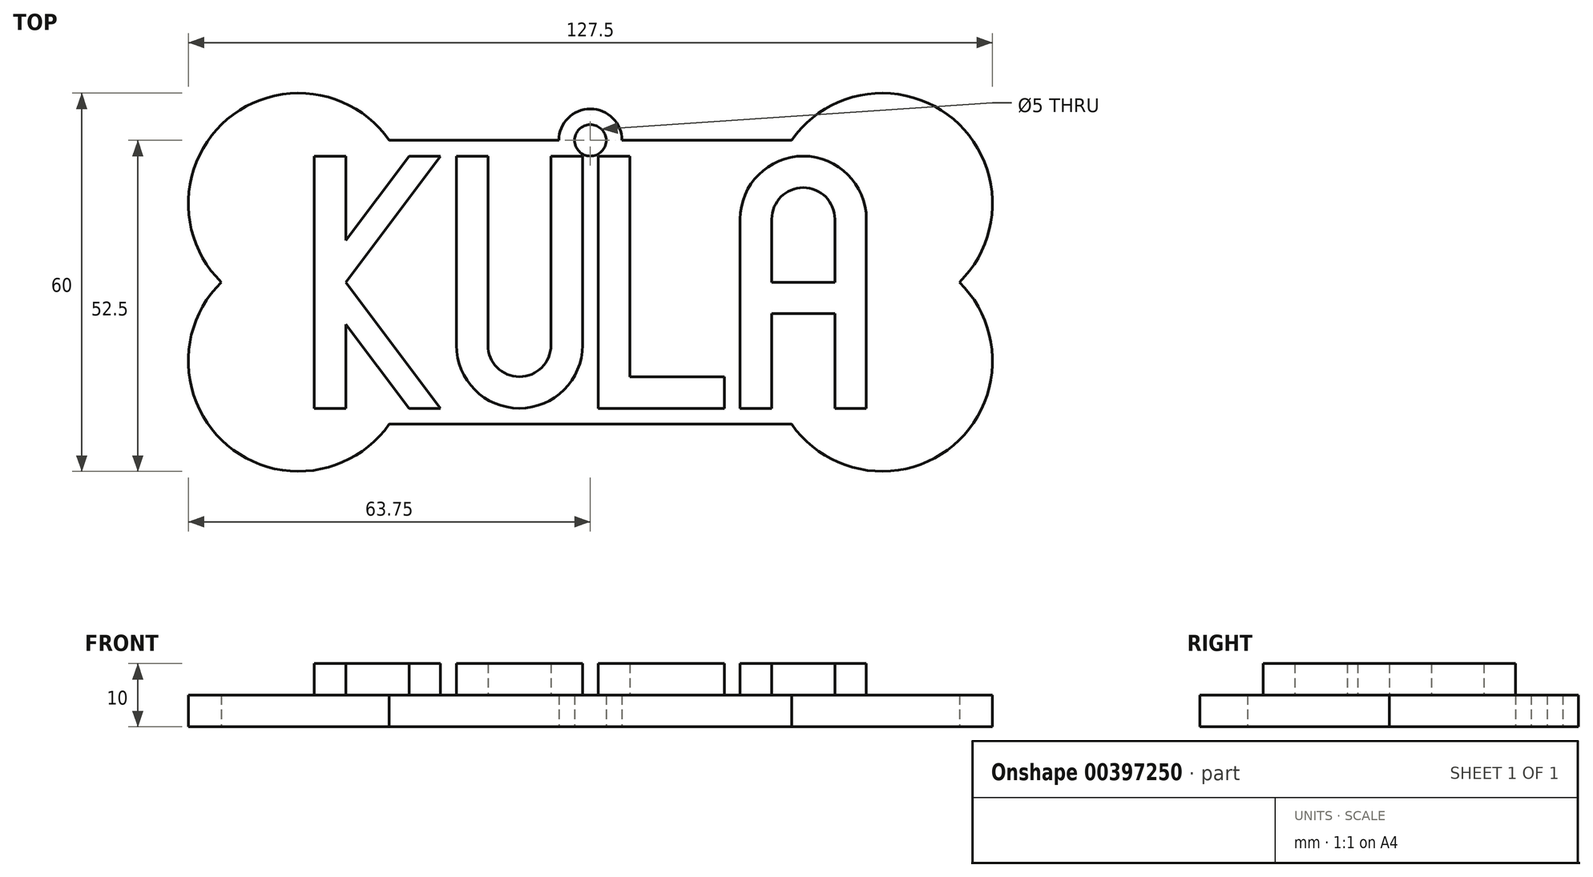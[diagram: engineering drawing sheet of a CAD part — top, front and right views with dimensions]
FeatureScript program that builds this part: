
annotation { "Feature Type Name" : "Feature", "Feature Type Description" : "" }
export const myFeature = defineFeature(function(context is Context, id is Id, definition is map)
    precondition{}
    {
        {
            var Q0;
            Q0=qCreatedBy(makeId("Top.planeOp"),FACE);
            var sketch = newSketch(context, id + "F0", { "sketchPlane" : qUnion([Q0])});
            skLineSegment(sketch, "E0.bottom", {"start": v(-90, 42.5) * mm, "end": v(-70, 42.5) * mm});
            skLineSegment(sketch, "E0.top", {"start": v(-90, 2.5) * mm, "end": v(-70, 2.5) * mm});
            skLineSegment(sketch, "E0.left", {"start": v(-90, 42.5) * mm, "end": v(-90, 2.5) * mm});
            skLineSegment(sketch, "E0.right", {"start": v(-70, 42.5) * mm, "end": v(-70, 2.5) * mm});
            skLineSegment(sketch, "E1.bottom", {"start": v(-67.5, 42.5) * mm, "end": v(-47.5, 42.5) * mm});
            skLineSegment(sketch, "E1.top", {"start": v(-67.5, 2.5) * mm, "end": v(-47.5, 2.5) * mm});
            skLineSegment(sketch, "E1.left", {"start": v(-67.5, 42.5) * mm, "end": v(-67.5, 2.5) * mm});
            skLineSegment(sketch, "E1.right", {"start": v(-47.5, 42.5) * mm, "end": v(-47.5, 2.5) * mm});
            skLineSegment(sketch, "E2.bottom", {"start": v(-22.5, 42.5) * mm, "end": v(-2.5, 42.5) * mm});
            skLineSegment(sketch, "E2.top", {"start": v(-22.5, 2.5) * mm, "end": v(-2.5, 2.5) * mm});
            skLineSegment(sketch, "E2.left", {"start": v(-22.5, 42.5) * mm, "end": v(-22.5, 2.5) * mm});
            skLineSegment(sketch, "E2.right", {"start": v(-2.5, 42.5) * mm, "end": v(-2.5, 2.5) * mm});
            skLineSegment(sketch, "E3.bottom", {"start": v(-92.5, 45) * mm, "end": v(0, 45) * mm});
            skLineSegment(sketch, "E3.top", {"start": v(-92.5, 0) * mm, "end": v(0, 0) * mm});
            skLineSegment(sketch, "E3.left", {"start": v(-92.5, 45) * mm, "end": v(-92.5, 0) * mm});
            skLineSegment(sketch, "E3.right", {"start": v(0, 45) * mm, "end": v(0, 0) * mm});
            skLineSegment(sketch, "E4.bottom", {"start": v(-45, 42.5) * mm, "end": v(-25, 42.5) * mm});
            skLineSegment(sketch, "E4.top", {"start": v(-45, 2.5) * mm, "end": v(-25, 2.5) * mm});
            skLineSegment(sketch, "E4.left", {"start": v(-45, 42.5) * mm, "end": v(-45, 2.5) * mm});
            skLineSegment(sketch, "E4.right", {"start": v(-25, 42.5) * mm, "end": v(-25, 2.5) * mm});
            skPoint(sketch, "E5", {"position": v(-92.5, 35) * mm});
            skPoint(sketch, "E6", {"position": v(-92.5, 10) * mm});
            skPoint(sketch, "E7", {"position": v(0, 10) * mm});
            skPoint(sketch, "E8", {"position": v(0, 35) * mm});
            skCircle(sketch, "E9", {"center": v(-92.5, 35) * mm, "radius": 17.5 * mm});
            skCircle(sketch, "E10", {"center": v(-92.5, 10) * mm, "radius": 17.5 * mm});
            skCircle(sketch, "E11", {"center": v(0, 35) * mm, "radius": 17.5 * mm});
            skCircle(sketch, "E12", {"center": v(0, 10) * mm, "radius": 17.5 * mm});
            skPoint(sketch, "E13", {"position": v(-46.25, 45) * mm});
            skCircle(sketch, "E14", {"center": v(-46.25, 45) * mm, "radius": 2.5 * mm});
            skCircle(sketch, "E15", {"center": v(-46.25, 45) * mm, "radius": 5 * mm});
            skSolve(sketch);
        }
        {
            var Q0;
            {var subQ0=sQuery(id+"F0.wireOp",EDGE,"E3.left");var subQ1=sQuery(id+"F0.wireOp",EDGE,"E3.bottom");var subQ2=makeQuery(id+"F0.imprint","INTERSECT",VERTEX,{"derivedFrom":[subQ1,subQ0]});Q0=makeQuery(id+"F0.imprint","IMPRINT",FACE,{"disambiguationData":[TD([[makeQuery(id+"F0.imprint","IMPRINT",EDGE,{"disambiguationData":[TD([[subQ2,-1.0]])],"derivedFrom":subQ1}),1.0]])]});}
            var Q1;
            {var subQ0=sQuery(id+"F0.wireOp",EDGE,"E10");var subQ1=sQuery(id+"F0.wireOp",EDGE,"E3.left");var subQ2=makeQuery(id+"F0.imprint","INTERSECT",VERTEX,{"derivedFrom":[subQ1,subQ0]});Q1=makeQuery(id+"F0.imprint","IMPRINT",FACE,{"disambiguationData":[TD([[makeQuery(id+"F0.imprint","IMPRINT",EDGE,{"disambiguationData":[TD([[subQ2,-1.0]])],"derivedFrom":subQ1}),-1.0]])]});}
            var Q2;
            {var subQ0=sQuery(id+"F0.wireOp",EDGE,"E3.left");var subQ1=sQuery(id+"F0.wireOp",EDGE,"E3.top");var subQ2=makeQuery(id+"F0.imprint","INTERSECT",VERTEX,{"derivedFrom":[subQ1,subQ0]});Q2=makeQuery(id+"F0.imprint","IMPRINT",FACE,{"disambiguationData":[TD([[makeQuery(id+"F0.imprint","IMPRINT",EDGE,{"disambiguationData":[TD([[subQ2,-1.0]])],"derivedFrom":subQ1}),-1.0]])]});}
            var Q3;
            {var subQ0=sQuery(id+"F0.wireOp",EDGE,"E10");var subQ1=sQuery(id+"F0.wireOp",EDGE,"E0.left");var subQ2=makeQuery(id+"F0.imprint","INTERSECT",VERTEX,{"derivedFrom":[subQ1,subQ0]});Q3=makeQuery(id+"F0.imprint","IMPRINT",FACE,{"disambiguationData":[TD([[makeQuery(id+"F0.imprint","IMPRINT",EDGE,{"disambiguationData":[TD([[subQ2,-1.0]])],"derivedFrom":subQ1}),-1.0]])]});}
            var Q4;
            {var subQ5=sQuery(id+"F0.wireOp",EDGE,"E0.left");var subQ6=sQuery(id+"F0.wireOp",EDGE,"E0.bottom");var subQ7=makeQuery(id+"F0.imprint","INTERSECT",VERTEX,{"derivedFrom":[subQ6,subQ5]});Q4=makeQuery(id+"F0.imprint","IMPRINT",FACE,{"disambiguationData":[TD([[makeQuery(id+"F0.imprint","IMPRINT",EDGE,{"disambiguationData":[TD([[subQ7,-1.0]])],"derivedFrom":subQ6}),1.0]])]});}
            var Q5;
            {var subQ0=sQuery(id+"F0.wireOp",EDGE,"E0.left");var subQ1=sQuery(id+"F0.wireOp",EDGE,"E0.bottom");var subQ2=makeQuery(id+"F0.imprint","INTERSECT",VERTEX,{"derivedFrom":[subQ1,subQ0]});Q5=makeQuery(id+"F0.imprint","IMPRINT",FACE,{"disambiguationData":[TD([[makeQuery(id+"F0.imprint","IMPRINT",EDGE,{"disambiguationData":[TD([[subQ2,-1.0]])],"derivedFrom":subQ1}),-1.0]])]});}
            var Q6;
            {var subQ0=sQuery(id+"F0.wireOp",EDGE,"E10");var subQ1=sQuery(id+"F0.wireOp",EDGE,"E0.left");var subQ2=makeQuery(id+"F0.imprint","INTERSECT",VERTEX,{"derivedFrom":[subQ1,subQ0]});Q6=makeQuery(id+"F0.imprint","IMPRINT",FACE,{"disambiguationData":[TD([[makeQuery(id+"F0.imprint","IMPRINT",EDGE,{"disambiguationData":[TD([[subQ2,-1.0]])],"derivedFrom":subQ1}),1.0]])]});}
            var Q7;
            {var subQ0=sQuery(id+"F0.wireOp",EDGE,"E0.left");var subQ1=sQuery(id+"F0.wireOp",EDGE,"E0.top");var subQ2=makeQuery(id+"F0.imprint","INTERSECT",VERTEX,{"derivedFrom":[subQ1,subQ0]});Q7=makeQuery(id+"F0.imprint","IMPRINT",FACE,{"disambiguationData":[TD([[makeQuery(id+"F0.imprint","IMPRINT",EDGE,{"disambiguationData":[TD([[subQ2,-1.0]])],"derivedFrom":subQ1}),1.0]])]});}
            var Q8;
            {var subQ5=sQuery(id+"F0.wireOp",EDGE,"E0.left");var subQ6=sQuery(id+"F0.wireOp",EDGE,"E0.top");var subQ7=makeQuery(id+"F0.imprint","INTERSECT",VERTEX,{"derivedFrom":[subQ6,subQ5]});Q8=makeQuery(id+"F0.imprint","IMPRINT",FACE,{"disambiguationData":[TD([[makeQuery(id+"F0.imprint","IMPRINT",EDGE,{"disambiguationData":[TD([[subQ7,-1.0]])],"derivedFrom":subQ6}),-1.0]])]});}
            var Q9;
            {var subQ0=sQuery(id+"F0.wireOp",EDGE,"E0.right");Q9=makeQuery(id+"F0.imprint","IMPRINT",FACE,{"disambiguationData":[TD([[makeQuery(id+"F0.imprint","IMPRINT",EDGE,{"derivedFrom":subQ0}),-1.0]])]});}
            var Q10;
            {var subQ9=sQuery(id+"F0.wireOp",EDGE,"E0.right");Q10=makeQuery(id+"F0.imprint","IMPRINT",FACE,{"disambiguationData":[TD([[makeQuery(id+"F0.imprint","IMPRINT",EDGE,{"derivedFrom":subQ9}),1.0]])]});}
            var Q11;
            Q11=makeQuery(id+"F0.imprint","IMPRINT",FACE,{"disambiguationData":[TD([[makeQuery(id+"F0.imprint","IMPRINT",EDGE,{"derivedFrom":sQuery(id+"F0.wireOp",EDGE,"E1.bottom")}),-1.0]])]});
            var Q12;
            Q12=makeQuery(id+"F0.imprint","IMPRINT",FACE,{"disambiguationData":[TD([[makeQuery(id+"F0.imprint","IMPRINT",EDGE,{"derivedFrom":sQuery(id+"F0.wireOp",EDGE,"E4.bottom")}),-1.0]])]});
            var Q13;
            {var subQ0=sQuery(id+"F0.wireOp",EDGE,"E2.left");Q13=makeQuery(id+"F0.imprint","IMPRINT",FACE,{"disambiguationData":[TD([[makeQuery(id+"F0.imprint","IMPRINT",EDGE,{"derivedFrom":subQ0}),1.0]])]});}
            var Q14;
            {var subQ0=sQuery(id+"F0.wireOp",EDGE,"E2.right");var subQ1=sQuery(id+"F0.wireOp",EDGE,"E2.bottom");var subQ2=makeQuery(id+"F0.imprint","INTERSECT",VERTEX,{"derivedFrom":[subQ1,subQ0]});Q14=makeQuery(id+"F0.imprint","IMPRINT",FACE,{"disambiguationData":[TD([[makeQuery(id+"F0.imprint","IMPRINT",EDGE,{"disambiguationData":[TD([[subQ2,1.0]])],"derivedFrom":subQ1}),-1.0]])]});}
            var Q15;
            {var subQ0=sQuery(id+"F0.wireOp",EDGE,"E3.right");var subQ1=sQuery(id+"F0.wireOp",EDGE,"E3.bottom");var subQ2=makeQuery(id+"F0.imprint","INTERSECT",VERTEX,{"derivedFrom":[subQ1,subQ0]});Q15=makeQuery(id+"F0.imprint","IMPRINT",FACE,{"disambiguationData":[TD([[makeQuery(id+"F0.imprint","IMPRINT",EDGE,{"disambiguationData":[TD([[subQ2,1.0]])],"derivedFrom":subQ1}),1.0]])]});}
            var Q16;
            {var subQ0=sQuery(id+"F0.wireOp",EDGE,"E3.right");var subQ1=sQuery(id+"F0.wireOp",EDGE,"E3.top");var subQ2=makeQuery(id+"F0.imprint","INTERSECT",VERTEX,{"derivedFrom":[subQ1,subQ0]});Q16=makeQuery(id+"F0.imprint","IMPRINT",FACE,{"disambiguationData":[TD([[makeQuery(id+"F0.imprint","IMPRINT",EDGE,{"disambiguationData":[TD([[subQ2,1.0]])],"derivedFrom":subQ1}),-1.0]])]});}
            var Q17;
            {var subQ0=sQuery(id+"F0.wireOp",EDGE,"E2.right");var subQ1=sQuery(id+"F0.wireOp",EDGE,"E2.top");var subQ2=makeQuery(id+"F0.imprint","INTERSECT",VERTEX,{"derivedFrom":[subQ1,subQ0]});Q17=makeQuery(id+"F0.imprint","IMPRINT",FACE,{"disambiguationData":[TD([[makeQuery(id+"F0.imprint","IMPRINT",EDGE,{"disambiguationData":[TD([[subQ2,1.0]])],"derivedFrom":subQ1}),1.0]])]});}
            var Q18;
            {var subQ0=sQuery(id+"F0.wireOp",EDGE,"E12");var subQ1=sQuery(id+"F0.wireOp",EDGE,"E2.right");var subQ2=makeQuery(id+"F0.imprint","INTERSECT",VERTEX,{"derivedFrom":[subQ1,subQ0]});Q18=makeQuery(id+"F0.imprint","IMPRINT",FACE,{"disambiguationData":[TD([[makeQuery(id+"F0.imprint","IMPRINT",EDGE,{"disambiguationData":[TD([[subQ2,-1.0]])],"derivedFrom":subQ1}),-1.0]])]});}
            var Q19;
            {var subQ0=sQuery(id+"F0.wireOp",EDGE,"E12");var subQ1=sQuery(id+"F0.wireOp",EDGE,"E3.right");var subQ2=makeQuery(id+"F0.imprint","INTERSECT",VERTEX,{"derivedFrom":[subQ1,subQ0]});Q19=makeQuery(id+"F0.imprint","IMPRINT",FACE,{"disambiguationData":[TD([[makeQuery(id+"F0.imprint","IMPRINT",EDGE,{"disambiguationData":[TD([[subQ2,-1.0]])],"derivedFrom":subQ1}),1.0]])]});}
            var Q20;
            {var subQ5=sQuery(id+"F0.wireOp",EDGE,"E2.right");var subQ6=sQuery(id+"F0.wireOp",EDGE,"E2.top");var subQ7=makeQuery(id+"F0.imprint","INTERSECT",VERTEX,{"derivedFrom":[subQ6,subQ5]});Q20=makeQuery(id+"F0.imprint","IMPRINT",FACE,{"disambiguationData":[TD([[makeQuery(id+"F0.imprint","IMPRINT",EDGE,{"disambiguationData":[TD([[subQ7,1.0]])],"derivedFrom":subQ6}),-1.0]])]});}
            var Q21;
            {var subQ7=sQuery(id+"F0.wireOp",EDGE,"E2.right");var subQ9=sQuery(id+"F0.wireOp",EDGE,"E2.bottom");var subQ10=makeQuery(id+"F0.imprint","INTERSECT",VERTEX,{"derivedFrom":[subQ9,subQ7]});Q21=makeQuery(id+"F0.imprint","IMPRINT",FACE,{"disambiguationData":[TD([[makeQuery(id+"F0.imprint","IMPRINT",EDGE,{"disambiguationData":[TD([[subQ10,1.0]])],"derivedFrom":subQ9}),1.0]])]});}
            var Q22;
            {var subQ0=sQuery(id+"F0.wireOp",EDGE,"E12");var subQ1=sQuery(id+"F0.wireOp",EDGE,"E2.right");var subQ2=makeQuery(id+"F0.imprint","INTERSECT",VERTEX,{"derivedFrom":[subQ1,subQ0]});Q22=makeQuery(id+"F0.imprint","IMPRINT",FACE,{"disambiguationData":[TD([[makeQuery(id+"F0.imprint","IMPRINT",EDGE,{"disambiguationData":[TD([[subQ2,-1.0]])],"derivedFrom":subQ1}),1.0]])]});}
            var Q23;
            {var subQ5=sQuery(id+"F0.wireOp",EDGE,"E1.right");var subQ6=sQuery(id+"F0.wireOp",EDGE,"E1.bottom");var subQ7=makeQuery(id+"F0.imprint","INTERSECT",VERTEX,{"derivedFrom":[subQ6,subQ5]});Q23=makeQuery(id+"F0.imprint","IMPRINT",FACE,{"disambiguationData":[TD([[makeQuery(id+"F0.imprint","IMPRINT",EDGE,{"disambiguationData":[TD([[subQ7,1.0]])],"derivedFrom":subQ6}),1.0]])]});}
            var Q24;
            {var subQ0=sQuery(id+"F0.wireOp",EDGE,"E15");var subQ1=sQuery(id+"F0.wireOp",EDGE,"E3.bottom");var subQ2=makeQuery(id+"F0.imprint","INTERSECT",VERTEX,{"disambiguationData":[OD(0.0)],"derivedFrom":[subQ1,subQ0]});Q24=makeQuery(id+"F0.imprint","IMPRINT",FACE,{"disambiguationData":[TD([[makeQuery(id+"F0.imprint","IMPRINT",EDGE,{"disambiguationData":[TD([[subQ2,-1.0]])],"derivedFrom":subQ1}),1.0]])]});}
            var Q25;
            {var subQ1=sQuery(id+"F0.wireOp",EDGE,"E1.top");Q25=makeQuery(id+"F0.imprint","IMPRINT",FACE,{"disambiguationData":[TD([[makeQuery(id+"F0.imprint","IMPRINT",EDGE,{"derivedFrom":subQ1}),1.0]])]});}
            var Q26;
            {var subQ2=sQuery(id+"F0.wireOp",EDGE,"E4.top");Q26=makeQuery(id+"F0.imprint","IMPRINT",FACE,{"disambiguationData":[TD([[makeQuery(id+"F0.imprint","IMPRINT",EDGE,{"derivedFrom":subQ2}),1.0]])]});}
            extrude(context, id + "F1", {"entities" : qUnion([Q0, Q1, Q2, Q3, Q4, Q5, Q6, Q7, Q8, Q9, Q10, Q11, Q12, Q13, Q14, Q15, Q16, Q17, Q18, Q19, Q20, Q21, Q22, Q23, Q24, Q25, Q26]), "depth" : 5 * mm});
        }
        {
            var Q0;
            Q0=makeQuery(id+"F1.opExtrude","CAP_FACE",FACE,{"disambiguationData":[OSD([sQuery(id+"F0.wireOp",EDGE,"E3.bottom"),sQuery(id+"F0.wireOp",EDGE,"E3.top"),sQuery(id+"F0.wireOp",EDGE,"E9"),sQuery(id+"F0.wireOp",EDGE,"E10"),sQuery(id+"F0.wireOp",EDGE,"E11"),sQuery(id+"F0.wireOp",EDGE,"E12")])],"isStart":false});
            var sketch = newSketch(context, id + "F2", { "sketchPlane" : qUnion([Q0])});
            skLineSegment(sketch, "E16.bottom", {"start": v(-90, 42.5) * mm, "end": v(-70, 42.5) * mm});
            skLineSegment(sketch, "E16.top", {"start": v(-90, 2.5) * mm, "end": v(-70, 2.5) * mm});
            skLineSegment(sketch, "E16.left", {"start": v(-90, 42.5) * mm, "end": v(-90, 2.5) * mm});
            skLineSegment(sketch, "E17.bottom", {"start": v(-67.5, 42.5) * mm, "end": v(-47.5, 42.5) * mm});
            skLineSegment(sketch, "E17.top", {"start": v(-67.5, 2.5) * mm, "end": v(-47.5, 2.5) * mm});
            skLineSegment(sketch, "E17.left", {"start": v(-67.5, 42.5) * mm, "end": v(-67.5, 2.5) * mm});
            skLineSegment(sketch, "E17.right", {"start": v(-47.5, 42.5) * mm, "end": v(-47.5, 2.5) * mm});
            skLineSegment(sketch, "E18.bottom", {"start": v(-22.5, 42.5) * mm, "end": v(-2.5, 42.5) * mm});
            skLineSegment(sketch, "E18.top", {"start": v(-22.5, 2.5) * mm, "end": v(-2.5, 2.5) * mm});
            skLineSegment(sketch, "E18.left", {"start": v(-22.5, 42.5) * mm, "end": v(-22.5, 2.5) * mm});
            skLineSegment(sketch, "E18.right", {"start": v(-2.5, 42.5) * mm, "end": v(-2.5, 2.5) * mm});
            skLineSegment(sketch, "E19.bottom", {"start": v(-92.5, 45) * mm, "end": v(0, 45) * mm});
            skLineSegment(sketch, "E19.top", {"start": v(-92.5, 0) * mm, "end": v(0, 0) * mm});
            skLineSegment(sketch, "E19.left", {"start": v(-92.5, 45) * mm, "end": v(-92.5, 0) * mm});
            skLineSegment(sketch, "E19.right", {"start": v(0, 45) * mm, "end": v(0, 0) * mm});
            skLineSegment(sketch, "E20.bottom", {"start": v(-45, 42.5) * mm, "end": v(-25, 42.5) * mm});
            skLineSegment(sketch, "E20.top", {"start": v(-45, 2.5) * mm, "end": v(-25, 2.5) * mm});
            skLineSegment(sketch, "E20.left", {"start": v(-45, 42.5) * mm, "end": v(-45, 2.5) * mm});
            skLineSegment(sketch, "E21", {"start": v(-70, 42.5) * mm, "end": v(-70, 2.5) * mm});
            skLineSegment(sketch, "E22", {"start": v(-25, 42.5) * mm, "end": v(-25, 2.5) * mm});
            skLineSegment(sketch, "E23", {"start": v(-85, 42.5) * mm, "end": v(-85, 2.5) * mm});
            skLineSegment(sketch, "E24", {"start": v(-62.5, 42.5) * mm, "end": v(-62.5, 2.5) * mm});
            skLineSegment(sketch, "E25", {"start": v(-40, 2.5) * mm, "end": v(-40, 42.5) * mm});
            skLineSegment(sketch, "E26", {"start": v(-45, 7.5) * mm, "end": v(-25, 7.5) * mm});
            skLineSegment(sketch, "E27", {"start": v(-17.5, 42.5) * mm, "end": v(-17.5, 2.5) * mm});
            skLineSegment(sketch, "E28", {"start": v(-22.5, 22.5) * mm, "end": v(-2.5, 22.5) * mm, "construction": true});
            skLineSegment(sketch, "E29", {"start": v(-2.5, 42.5) * mm, "end": v(-22.5, 22.5) * mm, "construction": true});
            skLineSegment(sketch, "E30", {"start": v(-22.5, 42.5) * mm, "end": v(-2.5, 22.5) * mm, "construction": true});
            skCircle(sketch, "E31", {"center": v(-12.5, 32.5) * mm, "radius": 10 * mm});
            skCircle(sketch, "E32", {"center": v(-12.5, 32.5) * mm, "radius": 5 * mm});
            skLineSegment(sketch, "E33", {"start": v(-52.5, 42.5) * mm, "end": v(-52.5, 2.5) * mm});
            skLineSegment(sketch, "E34", {"start": v(-67.5, 22.5) * mm, "end": v(-47.5, 22.5) * mm, "construction": true});
            skLineSegment(sketch, "E35", {"start": v(-67.5, 22.5) * mm, "end": v(-47.5, 2.5) * mm, "construction": true});
            skLineSegment(sketch, "E36", {"start": v(-47.5, 22.5) * mm, "end": v(-67.5, 2.5) * mm, "construction": true});
            skLineSegment(sketch, "E37", {"start": v(-7.5, 42.5) * mm, "end": v(-7.5, 2.5) * mm});
            skLineSegment(sketch, "E38", {"start": v(-22.5, 22.5) * mm, "end": v(-2.5, 22.5) * mm});
            skLineSegment(sketch, "E39", {"start": v(-22.5, 17.5) * mm, "end": v(-2.5, 17.5) * mm});
            skCircle(sketch, "E40", {"center": v(-57.5, 12.5) * mm, "radius": 10 * mm});
            skCircle(sketch, "E41", {"center": v(-57.5, 12.5) * mm, "radius": 5 * mm});
            skLineSegment(sketch, "E42", {"start": v(-90, 22.5) * mm, "end": v(-70, 22.5) * mm, "construction": true});
            skLineSegment(sketch, "E43", {"start": v(-70, 42.5) * mm, "end": v(-85, 22.5) * mm});
            skLineSegment(sketch, "E44", {"start": v(-85, 22.5) * mm, "end": v(-70, 2.5) * mm});
            skLineSegment(sketch, "E45", {"start": v(-90, 22.5) * mm, "end": v(-75, 2.5) * mm});
            skLineSegment(sketch, "E46", {"start": v(-90, 22.5) * mm, "end": v(-75, 42.5) * mm});
            skSolve(sketch);
        }
        {
            var Q0;
            {var subQ0=sQuery(id+"F2.wireOp",EDGE,"E16.left");var subQ1=sQuery(id+"F2.wireOp",EDGE,"E16.bottom");var subQ2=makeQuery(id+"F2.imprint","INTERSECT",VERTEX,{"derivedFrom":[subQ1,subQ0]});Q0=makeQuery(id+"F2.imprint","IMPRINT",FACE,{"disambiguationData":[TD([[makeQuery(id+"F2.imprint","IMPRINT",EDGE,{"disambiguationData":[TD([[subQ2,-1.0]])],"derivedFrom":subQ1}),-1.0]])]});}
            var Q1;
            {var subQ0=sQuery(id+"F2.wireOp",EDGE,"E23");var subQ2=sQuery(id+"F2.wireOp",EDGE,"E46");var subQ3=makeQuery(id+"F2.imprint","INTERSECT",VERTEX,{"derivedFrom":[subQ0,subQ2]});Q1=makeQuery(id+"F2.imprint","IMPRINT",FACE,{"disambiguationData":[TD([[makeQuery(id+"F2.imprint","IMPRINT",EDGE,{"disambiguationData":[TD([[subQ3,-1.0]])],"derivedFrom":subQ0}),-1.0]])]});}
            var Q2;
            {var subQ0=sQuery(id+"F2.wireOp",EDGE,"E16.left");var subQ1=sQuery(id+"F2.wireOp",EDGE,"E16.top");var subQ2=makeQuery(id+"F2.imprint","INTERSECT",VERTEX,{"derivedFrom":[subQ1,subQ0]});Q2=makeQuery(id+"F2.imprint","IMPRINT",FACE,{"disambiguationData":[TD([[makeQuery(id+"F2.imprint","IMPRINT",EDGE,{"disambiguationData":[TD([[subQ2,-1.0]])],"derivedFrom":subQ1}),1.0]])]});}
            var Q3;
            {var subQ0=sQuery(id+"F2.wireOp",EDGE,"E44");Q3=makeQuery(id+"F2.imprint","IMPRINT",FACE,{"disambiguationData":[TD([[makeQuery(id+"F2.imprint","IMPRINT",EDGE,{"derivedFrom":subQ0}),-1.0]])]});}
            var Q4;
            {var subQ0=sQuery(id+"F2.wireOp",EDGE,"E43");Q4=makeQuery(id+"F2.imprint","IMPRINT",FACE,{"disambiguationData":[TD([[makeQuery(id+"F2.imprint","IMPRINT",EDGE,{"derivedFrom":subQ0}),-1.0]])]});}
            var Q5;
            {var subQ0=sQuery(id+"F2.wireOp",EDGE,"E17.left");var subQ1=sQuery(id+"F2.wireOp",EDGE,"E17.bottom");var subQ2=makeQuery(id+"F2.imprint","INTERSECT",VERTEX,{"derivedFrom":[subQ1,subQ0]});Q5=makeQuery(id+"F2.imprint","IMPRINT",FACE,{"disambiguationData":[TD([[makeQuery(id+"F2.imprint","IMPRINT",EDGE,{"disambiguationData":[TD([[subQ2,-1.0]])],"derivedFrom":subQ1}),-1.0]])]});}
            var Q6;
            {var subQ0=sQuery(id+"F2.wireOp",EDGE,"E40");var subQ1=sQuery(id+"F2.wireOp",EDGE,"E24");var subQ2=makeQuery(id+"F2.imprint","INTERSECT",VERTEX,{"disambiguationData":[OD(0.0)],"derivedFrom":[subQ1,subQ0]});Q6=makeQuery(id+"F2.imprint","IMPRINT",FACE,{"disambiguationData":[TD([[makeQuery(id+"F2.imprint","IMPRINT",EDGE,{"disambiguationData":[TD([[subQ2,-1.0]])],"derivedFrom":subQ1}),-1.0]])]});}
            var Q7;
            {var subQ2=sQuery(id+"F2.wireOp",EDGE,"E24");var subQ6=sQuery(id+"F2.wireOp",EDGE,"E41");var subQ7=makeQuery(id+"F2.imprint","INTERSECT",VERTEX,{"derivedFrom":[subQ2,subQ6]});Q7=makeQuery(id+"F2.imprint","IMPRINT",FACE,{"disambiguationData":[TD([[makeQuery(id+"F2.imprint","IMPRINT",EDGE,{"disambiguationData":[TD([[subQ7,-1.0]])],"derivedFrom":subQ2}),1.0]])]});}
            var Q8;
            {var subQ0=sQuery(id+"F2.wireOp",EDGE,"E40");var subQ1=sQuery(id+"F2.wireOp",EDGE,"E33");var subQ2=makeQuery(id+"F2.imprint","INTERSECT",VERTEX,{"disambiguationData":[OD(0.0)],"derivedFrom":[subQ1,subQ0]});Q8=makeQuery(id+"F2.imprint","IMPRINT",FACE,{"disambiguationData":[TD([[makeQuery(id+"F2.imprint","IMPRINT",EDGE,{"disambiguationData":[TD([[subQ2,-1.0]])],"derivedFrom":subQ1}),1.0]])]});}
            var Q9;
            {var subQ0=sQuery(id+"F2.wireOp",EDGE,"E17.right");var subQ1=sQuery(id+"F2.wireOp",EDGE,"E17.bottom");var subQ2=makeQuery(id+"F2.imprint","INTERSECT",VERTEX,{"derivedFrom":[subQ1,subQ0]});Q9=makeQuery(id+"F2.imprint","IMPRINT",FACE,{"disambiguationData":[TD([[makeQuery(id+"F2.imprint","IMPRINT",EDGE,{"disambiguationData":[TD([[subQ2,1.0]])],"derivedFrom":subQ1}),-1.0]])]});}
            var Q10;
            {var subQ0=sQuery(id+"F2.wireOp",EDGE,"E20.left");var subQ1=sQuery(id+"F2.wireOp",EDGE,"E20.bottom");var subQ2=makeQuery(id+"F2.imprint","INTERSECT",VERTEX,{"derivedFrom":[subQ1,subQ0]});Q10=makeQuery(id+"F2.imprint","IMPRINT",FACE,{"disambiguationData":[TD([[makeQuery(id+"F2.imprint","IMPRINT",EDGE,{"disambiguationData":[TD([[subQ2,-1.0]])],"derivedFrom":subQ1}),-1.0]])]});}
            var Q11;
            {var subQ0=sQuery(id+"F2.wireOp",EDGE,"E20.left");var subQ1=sQuery(id+"F2.wireOp",EDGE,"E20.top");var subQ2=makeQuery(id+"F2.imprint","INTERSECT",VERTEX,{"derivedFrom":[subQ1,subQ0]});Q11=makeQuery(id+"F2.imprint","IMPRINT",FACE,{"disambiguationData":[TD([[makeQuery(id+"F2.imprint","IMPRINT",EDGE,{"disambiguationData":[TD([[subQ2,-1.0]])],"derivedFrom":subQ1}),1.0]])]});}
            var Q12;
            {var subQ0=sQuery(id+"F2.wireOp",EDGE,"E22");var subQ1=sQuery(id+"F2.wireOp",EDGE,"E20.top");var subQ2=makeQuery(id+"F2.imprint","INTERSECT",VERTEX,{"derivedFrom":[subQ1,subQ0]});Q12=makeQuery(id+"F2.imprint","IMPRINT",FACE,{"disambiguationData":[TD([[makeQuery(id+"F2.imprint","IMPRINT",EDGE,{"disambiguationData":[TD([[subQ2,1.0]])],"derivedFrom":subQ1}),1.0]])]});}
            var Q13;
            {var subQ0=sQuery(id+"F2.wireOp",EDGE,"E31");var subQ1=sQuery(id+"F2.wireOp",EDGE,"E27");var subQ2=makeQuery(id+"F2.imprint","INTERSECT",VERTEX,{"disambiguationData":[OD(0.0)],"derivedFrom":[subQ1,subQ0]});Q13=makeQuery(id+"F2.imprint","IMPRINT",FACE,{"disambiguationData":[TD([[makeQuery(id+"F2.imprint","IMPRINT",EDGE,{"disambiguationData":[TD([[subQ2,-1.0]])],"derivedFrom":subQ1}),-1.0]])]});}
            var Q14;
            {var subQ1=sQuery(id+"F2.wireOp",EDGE,"E27");var subQ5=sQuery(id+"F2.wireOp",EDGE,"E31");var subQ7=makeQuery(id+"F2.imprint","INTERSECT",VERTEX,{"disambiguationData":[OD(0.0)],"derivedFrom":[subQ1,subQ5]});Q14=makeQuery(id+"F2.imprint","IMPRINT",FACE,{"disambiguationData":[TD([[makeQuery(id+"F2.imprint","IMPRINT",EDGE,{"disambiguationData":[TD([[subQ7,-1.0]])],"derivedFrom":subQ1}),1.0]])]});}
            var Q15;
            {var subQ0=sQuery(id+"F2.wireOp",EDGE,"E31");var subQ1=makeQuery(id+"F2.imprint","INTERSECT",VERTEX,{"derivedFrom":[sQuery(id+"F2.wireOp",EDGE,"E18.right"),subQ0]});Q15=makeQuery(id+"F2.imprint","IMPRINT",FACE,{"disambiguationData":[TD([[makeQuery(id+"F2.imprint","IMPRINT",EDGE,{"disambiguationData":[TD([[subQ1,-1.0]])],"derivedFrom":subQ0}),1.0]])]});}
            var Q16;
            {var subQ0=sQuery(id+"F2.wireOp",EDGE,"E38");var subQ4=sQuery(id+"F2.wireOp",EDGE,"E27");var subQ5=makeQuery(id+"F2.imprint","INTERSECT",VERTEX,{"derivedFrom":[subQ4,subQ0]});Q16=makeQuery(id+"F2.imprint","IMPRINT",FACE,{"disambiguationData":[TD([[makeQuery(id+"F2.imprint","IMPRINT",EDGE,{"disambiguationData":[TD([[subQ5,-1.0]])],"derivedFrom":subQ4}),1.0]])]});}
            var Q17;
            {var subQ0=sQuery(id+"F2.wireOp",EDGE,"E38");var subQ1=sQuery(id+"F2.wireOp",EDGE,"E18.left");var subQ2=makeQuery(id+"F2.imprint","INTERSECT",VERTEX,{"derivedFrom":[subQ1,subQ0]});Q17=makeQuery(id+"F2.imprint","IMPRINT",FACE,{"disambiguationData":[TD([[makeQuery(id+"F2.imprint","IMPRINT",EDGE,{"disambiguationData":[TD([[subQ2,-1.0]])],"derivedFrom":subQ1}),1.0]])]});}
            var Q18;
            {var subQ0=sQuery(id+"F2.wireOp",EDGE,"E38");var subQ1=sQuery(id+"F2.wireOp",EDGE,"E18.left");var subQ2=makeQuery(id+"F2.imprint","INTERSECT",VERTEX,{"derivedFrom":[subQ1,subQ0]});Q18=makeQuery(id+"F2.imprint","IMPRINT",FACE,{"disambiguationData":[TD([[makeQuery(id+"F2.imprint","IMPRINT",EDGE,{"disambiguationData":[TD([[subQ2,1.0]])],"derivedFrom":subQ1}),1.0]])]});}
            var Q19;
            {var subQ0=sQuery(id+"F2.wireOp",EDGE,"E38");var subQ1=sQuery(id+"F2.wireOp",EDGE,"E18.right");var subQ2=makeQuery(id+"F2.imprint","INTERSECT",VERTEX,{"derivedFrom":[subQ1,subQ0]});Q19=makeQuery(id+"F2.imprint","IMPRINT",FACE,{"disambiguationData":[TD([[makeQuery(id+"F2.imprint","IMPRINT",EDGE,{"disambiguationData":[TD([[subQ2,1.0]])],"derivedFrom":subQ1}),-1.0]])]});}
            var Q20;
            {var subQ0=sQuery(id+"F2.wireOp",EDGE,"E38");var subQ1=sQuery(id+"F2.wireOp",EDGE,"E18.right");var subQ2=makeQuery(id+"F2.imprint","INTERSECT",VERTEX,{"derivedFrom":[subQ1,subQ0]});Q20=makeQuery(id+"F2.imprint","IMPRINT",FACE,{"disambiguationData":[TD([[makeQuery(id+"F2.imprint","IMPRINT",EDGE,{"disambiguationData":[TD([[subQ2,-1.0]])],"derivedFrom":subQ1}),-1.0]])]});}
            var Q21;
            {var subQ0=sQuery(id+"F2.wireOp",EDGE,"E18.right");var subQ1=sQuery(id+"F2.wireOp",EDGE,"E18.top");var subQ2=makeQuery(id+"F2.imprint","INTERSECT",VERTEX,{"derivedFrom":[subQ1,subQ0]});Q21=makeQuery(id+"F2.imprint","IMPRINT",FACE,{"disambiguationData":[TD([[makeQuery(id+"F2.imprint","IMPRINT",EDGE,{"disambiguationData":[TD([[subQ2,1.0]])],"derivedFrom":subQ1}),1.0]])]});}
            var Q22;
            {var subQ0=sQuery(id+"F2.wireOp",EDGE,"E18.left");var subQ1=sQuery(id+"F2.wireOp",EDGE,"E18.top");var subQ2=makeQuery(id+"F2.imprint","INTERSECT",VERTEX,{"derivedFrom":[subQ1,subQ0]});Q22=makeQuery(id+"F2.imprint","IMPRINT",FACE,{"disambiguationData":[TD([[makeQuery(id+"F2.imprint","IMPRINT",EDGE,{"disambiguationData":[TD([[subQ2,-1.0]])],"derivedFrom":subQ1}),1.0]])]});}
            extrude(context, id + "F3", {"entities" : qUnion([Q0, Q1, Q2, Q3, Q4, Q5, Q6, Q7, Q8, Q9, Q10, Q11, Q12, Q13, Q14, Q15, Q16, Q17, Q18, Q19, Q20, Q21, Q22]), "operationType" : NewBodyOperationType.ADD, "depth" : 5 * mm});
        }
    });
